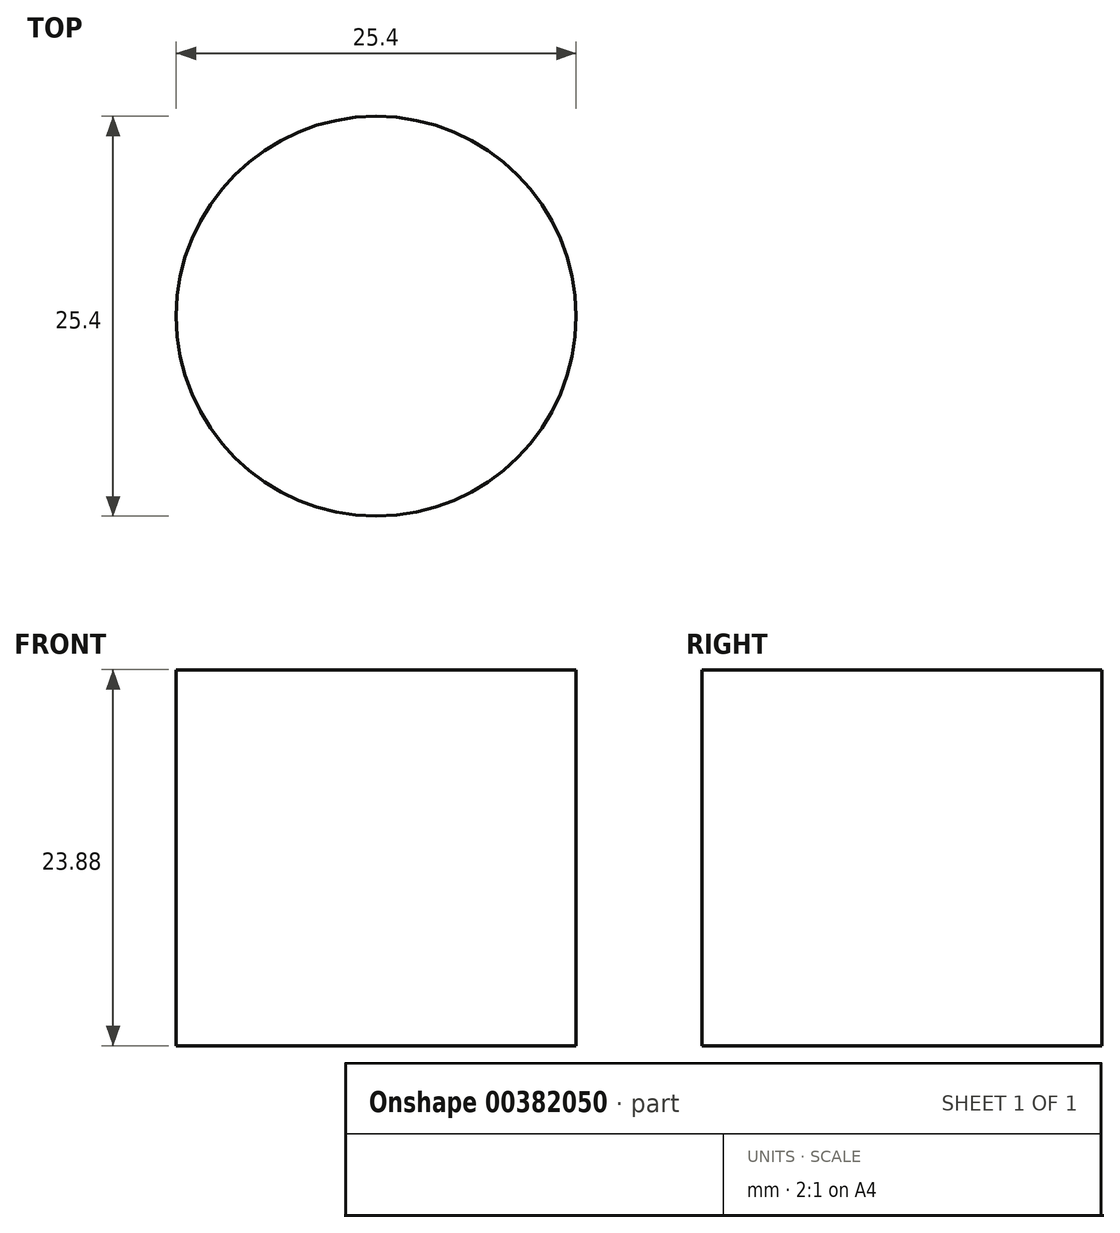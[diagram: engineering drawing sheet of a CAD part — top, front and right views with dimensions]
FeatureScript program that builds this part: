
annotation { "Feature Type Name" : "Feature", "Feature Type Description" : "" }
export const myFeature = defineFeature(function(context is Context, id is Id, definition is map)
    precondition{}
    {
        {
            var Q0;
            Q0=qCreatedBy(makeId("Top.planeOp"),FACE);
            var sketch = newSketch(context, id + "F0", { "sketchPlane" : qUnion([Q0])});
            skCircle(sketch, "E0", {"center": v(0, 0) * mm, "radius": 12.7 * mm});
            skSolve(sketch);
        }
        {
            var Q0;
            Q0=makeQuery(id+"F0.imprint","IMPRINT",FACE,{"disambiguationData":[TD([[makeQuery(id+"F0.imprint","IMPRINT",EDGE,{"derivedFrom":sQuery(id+"F0.wireOp",EDGE,"E0")}),1.0]])]});
            extrude(context, id + "F1", {"entities" : qUnion([Q0]), "depth" : 23.88 * mm});
        }
    });
